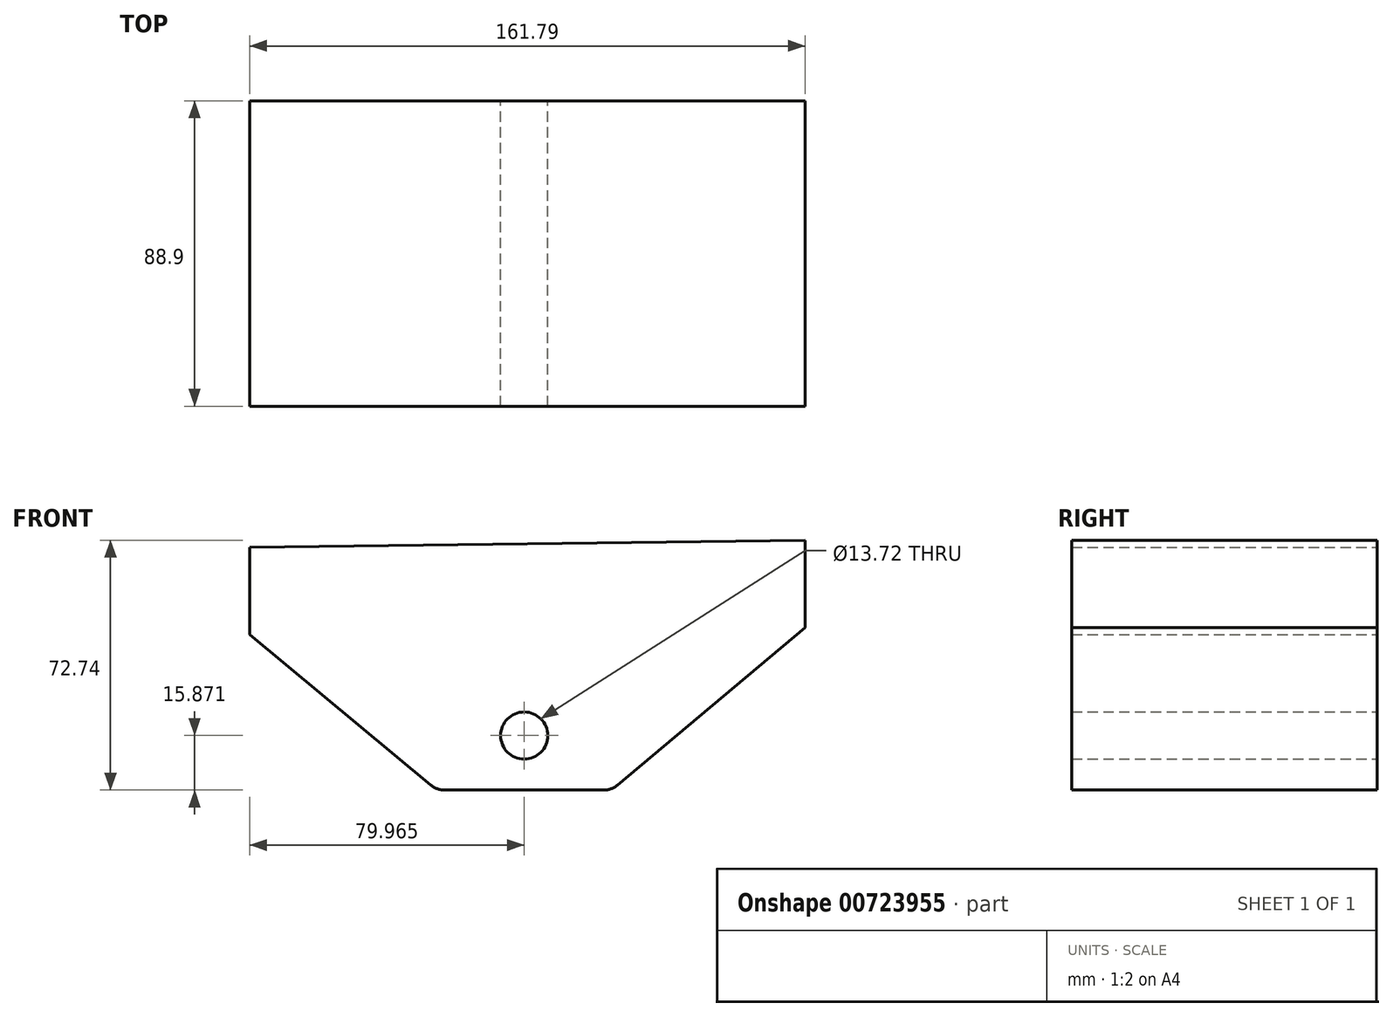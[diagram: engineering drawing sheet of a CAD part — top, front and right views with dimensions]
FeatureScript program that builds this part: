
annotation { "Feature Type Name" : "Feature", "Feature Type Description" : "" }
export const myFeature = defineFeature(function(context is Context, id is Id, definition is map)
    precondition{}
    {
        {
            var Q0;
            Q0=qCreatedBy(makeId("Front.planeOp"),FACE);
            var sketch = newSketch(context, id + "F0", { "sketchPlane" : qUnion([Q0])});
            skCircle(sketch, "E0", {"center": v(19.16, -27.88) * mm, "radius": 6.86 * mm});
            skLineSegment(sketch, "E1", {"start": v(19.16, -43.75) * mm, "end": v(42.24, -43.75) * mm});
            skLineSegment(sketch, "E2", {"start": v(19.16, -43.75) * mm, "end": v(-3.96, -43.75) * mm});
            skLineSegment(sketch, "E3", {"start": v(19.16, -27.88) * mm, "end": v(19.16, -43.75) * mm, "construction": true});
            skLineSegment(sketch, "E4", {"start": v(74, 114.66) * mm, "end": v(40.98, 114.66) * mm});
            skLineSegment(sketch, "E5", {"start": v(-60.8, 1.47) * mm, "end": v(-8, -42.3) * mm});
            skLineSegment(sketch, "E6", {"start": v(40.98, 114.66) * mm, "end": v(-35.98, 114.66) * mm});
            skPoint(sketch, "E7.visualSharp", {"position": v(74, 114.66) * mm});
            skPoint(sketch, "E8.visualSharp", {"position": v(100.98, 3.6) * mm});
            skPoint(sketch, "E9.visualSharp", {"position": v(44.56, -43.75) * mm});
            skArc(sketch, "E9.filletArc", {"start": v(42.24, -43.75) * mm, "mid": v(44.42, -43.37) * mm, "end": v(46.33, -42.27) * mm});
            skPoint(sketch, "E10.visualSharp", {"position": v(43.4, -40.58) * mm});
            skPoint(sketch, "E11.visualSharp", {"position": v(-5.1, -40.58) * mm});
            skPoint(sketch, "E12.visualSharp", {"position": v(-6.24, -43.75) * mm});
            skArc(sketch, "E12.filletArc", {"start": v(-8, -42.3) * mm, "mid": v(-6.1, -43.38) * mm, "end": v(-3.96, -43.75) * mm});
            skLineSegment(sketch, "E13", {"start": v(-60.8, 1.47) * mm, "end": v(-60.8, 52.27) * mm});
            skLineSegment(sketch, "E14", {"start": v(-60.8, 52.27) * mm, "end": v(-35.98, 114.66) * mm});
            skLineSegment(sketch, "E15", {"start": v(100.98, 3.6) * mm, "end": v(100.98, 54.4) * mm});
            skLineSegment(sketch, "E16", {"start": v(74, 114.66) * mm, "end": v(100.98, 54.4) * mm});
            skLineSegment(sketch, "E17", {"start": v(46.33, -42.27) * mm, "end": v(100.98, 3.6) * mm});
            skLineSegment(sketch, "E18", {"start": v(-60.8, 26.87) * mm, "end": v(100.98, 29) * mm});
            skSolve(sketch);
        }
        {
            var Q0;
            Q0=makeQuery(id+"F0.imprint","IMPRINT",FACE,{"disambiguationData":[TD([[makeQuery(id+"F0.imprint","IMPRINT",EDGE,{"derivedFrom":sQuery(id+"F0.wireOp",EDGE,"E0")}),-1.0]])]});
            extrude(context, id + "F1", {"entities" : qUnion([Q0]), "depth" : 3.17 * mm, "offsetDistance" : 25.4 * mm});
        }
        {
            var Q0;
            Q0=makeQuery(id+"F0.imprint","IMPRINT",FACE,{"disambiguationData":[TD([[makeQuery(id+"F0.imprint","IMPRINT",EDGE,{"derivedFrom":sQuery(id+"F0.wireOp",EDGE,"E1")}),1.0]])]});
            extrude(context, id + "F2", {"entities" : qUnion([Q0]), "operationType" : NewBodyOperationType.ADD, "depth" : 88.9 * mm, "offsetDistance" : 25.4 * mm});
        }
    });
